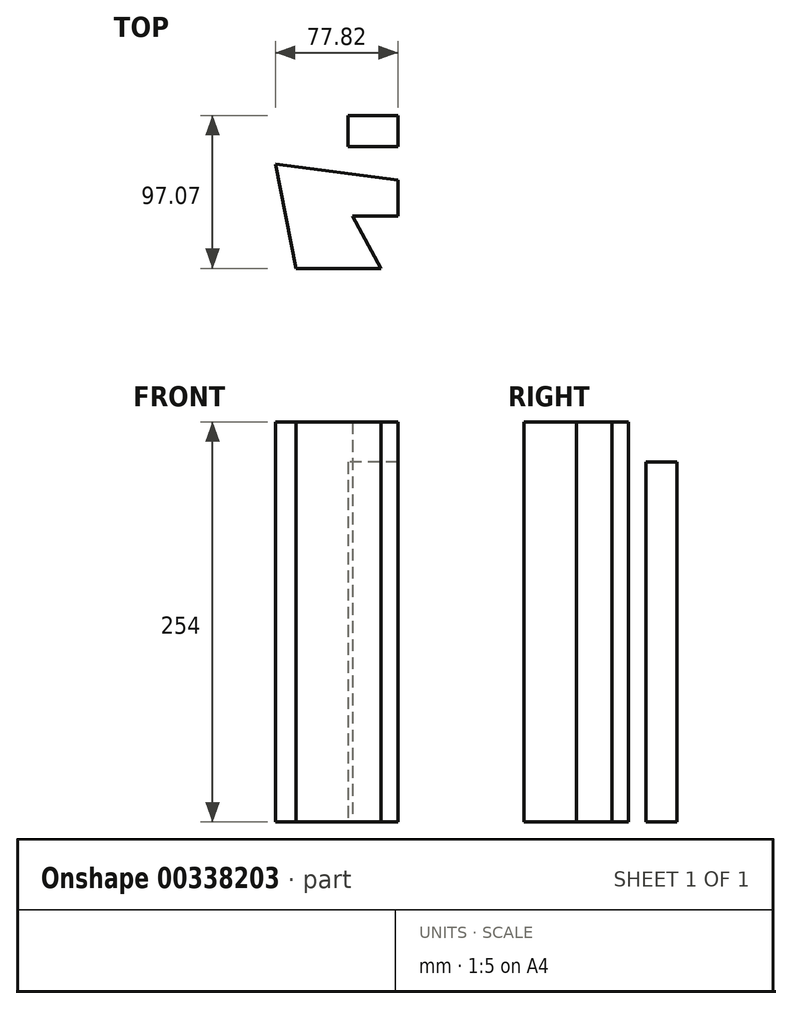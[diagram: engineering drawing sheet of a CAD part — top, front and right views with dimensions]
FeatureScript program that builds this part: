
annotation { "Feature Type Name" : "Feature", "Feature Type Description" : "" }
export const myFeature = defineFeature(function(context is Context, id is Id, definition is map)
    precondition{}
    {
        {
            var Q0;
            Q0=qCreatedBy(makeId("Top.planeOp"),FACE);
            var sketch = newSketch(context, id + "F0", { "sketchPlane" : qUnion([Q0])});
            skLineSegment(sketch, "E0", {"start": v(27.37, -33.37) * mm, "end": v(-26.36, -33.37) * mm});
            skLineSegment(sketch, "E1", {"start": v(-26.36, -33.37) * mm, "end": v(-39.54, 33.04) * mm});
            skLineSegment(sketch, "E2", {"start": v(-39.54, 33.04) * mm, "end": v(38.28, 22.67) * mm});
            skLineSegment(sketch, "E3", {"start": v(38.28, 22.67) * mm, "end": v(38.28, 0) * mm});
            skLineSegment(sketch, "E4", {"start": v(38.28, 0) * mm, "end": v(9.49, 0) * mm});
            skLineSegment(sketch, "E5", {"start": v(9.49, 0) * mm, "end": v(27.37, -33.37) * mm});
            skLineSegment(sketch, "E6", {"start": v(38.28, 44.03) * mm, "end": v(6.68, 44.03) * mm});
            skLineSegment(sketch, "E7", {"start": v(6.68, 44.03) * mm, "end": v(6.68, 63.7) * mm});
            skLineSegment(sketch, "E8", {"start": v(6.68, 63.7) * mm, "end": v(38.28, 63.7) * mm});
            skLineSegment(sketch, "E9", {"start": v(38.28, 63.7) * mm, "end": v(38.28, 44.03) * mm});
            skLineSegment(sketch, "E10", {"start": v(-46.2, -35.19) * mm, "end": v(-40.04, 190.7) * mm});
            skSolve(sketch);
        }
        {
            var Q0;
            Q0 = qSketchRegion(id + "F0", true);
            extrude(context, id + "F1", {"entities" : qUnion([Q0]), "depth" : 228.6 * mm});
        }
        {
            var Q0;
            Q0=makeQuery(id+"F1.opExtrude","CAP_FACE",FACE,{"disambiguationData":[OSD([sQuery(id+"F0.wireOp",EDGE,"E0"),sQuery(id+"F0.wireOp",EDGE,"E1"),sQuery(id+"F0.wireOp",EDGE,"E2"),sQuery(id+"F0.wireOp",EDGE,"E3"),sQuery(id+"F0.wireOp",EDGE,"E4"),sQuery(id+"F0.wireOp",EDGE,"E5")])],"isStart":false});
            extrude(context, id + "F2", {"entities" : qUnion([Q0]), "operationType" : NewBodyOperationType.ADD, "depth" : 25.4 * mm});
        }
    });
